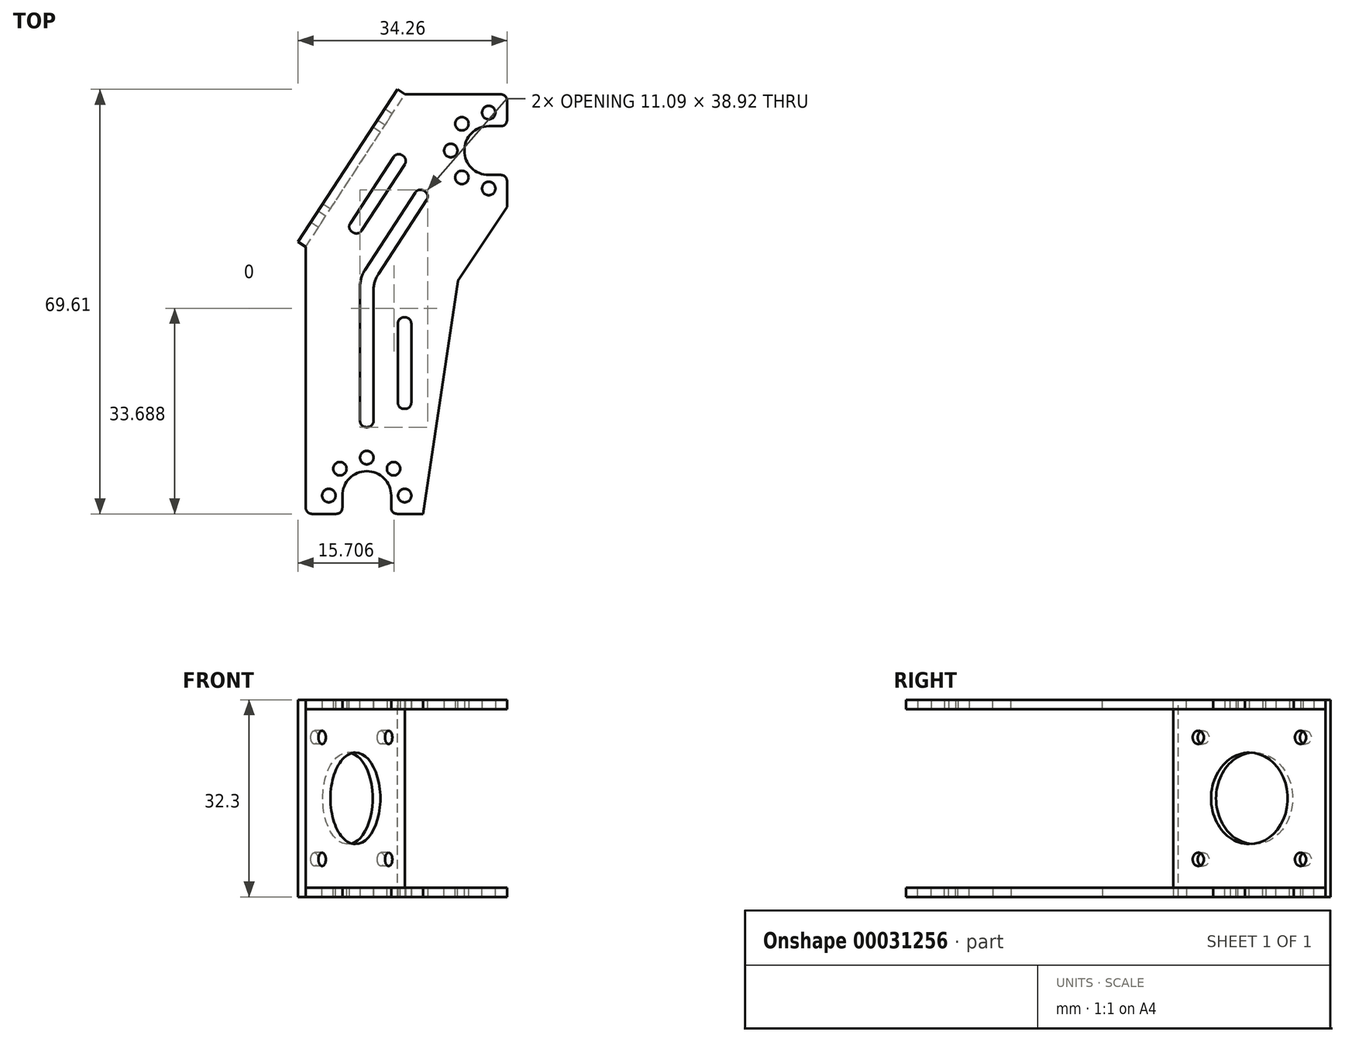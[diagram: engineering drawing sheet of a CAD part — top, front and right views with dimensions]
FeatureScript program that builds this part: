
annotation { "Feature Type Name" : "Feature", "Feature Type Description" : "" }
export const myFeature = defineFeature(function(context is Context, id is Id, definition is map)
    precondition{}
    {
        {
            var Q0;
            Q0=qCreatedBy(makeId("Top.planeOp"),FACE);
            var sketch = newSketch(context, id + "F0", { "sketchPlane" : qUnion([Q0])});
            skLineSegment(sketch, "E0.bottom", {"start": v(-16.5, 34.4) * mm, "end": v(16.5, 34.4) * mm});
            skLineSegment(sketch, "E0.top", {"start": v(-16.5, -34.4) * mm, "end": v(-10.5, -34.4) * mm});
            skLineSegment(sketch, "E0.left", {"start": v(-16.5, 34.4) * mm, "end": v(-16.5, -34.4) * mm});
            skLineSegment(sketch, "E0.right", {"start": v(16.5, 34.4) * mm, "end": v(16.5, 29.17) * mm});
            skPoint(sketch, "E0.middle", {"position": v(0, 0) * mm});
            skArc(sketch, "E1", {"start": v(13.5, 29.17) * mm, "mid": v(9.5, 25.17) * mm, "end": v(13.5, 21.17) * mm});
            skArc(sketch, "E2", {"start": v(-2.5, -31.4) * mm, "mid": v(-6.5, -27.4) * mm, "end": v(-10.5, -31.4) * mm});
            skLineSegment(sketch, "E3.bottom", {"start": v(9.1, 29.57) * mm, "end": v(17.9, 29.57) * mm, "construction": true});
            skLineSegment(sketch, "E3.top", {"start": v(9.1, 20.77) * mm, "end": v(17.9, 20.77) * mm, "construction": true});
            skLineSegment(sketch, "E3.left", {"start": v(9.1, 29.57) * mm, "end": v(9.1, 20.77) * mm, "construction": true});
            skLineSegment(sketch, "E3.right", {"start": v(17.9, 29.57) * mm, "end": v(17.9, 20.77) * mm, "construction": true});
            skCircle(sketch, "E4", {"center": v(9.1, 29.57) * mm, "radius": 1.1 * mm});
            skCircle(sketch, "E5.1.0", {"center": v(7.28, 25.17) * mm, "radius": 1.1 * mm});
            skCircle(sketch, "E5.2.0", {"center": v(9.1, 20.77) * mm, "radius": 1.1 * mm});
            skCircle(sketch, "E5.3.0", {"center": v(13.5, 18.95) * mm, "radius": 1.1 * mm});
            skCircle(sketch, "E5.7.0", {"center": v(13.5, 31.4) * mm, "radius": 1.1 * mm});
            skLineSegment(sketch, "E6.bottom", {"start": v(-10.9, -27) * mm, "end": v(-2.1, -27) * mm, "construction": true});
            skLineSegment(sketch, "E6.top", {"start": v(-10.9, -35.8) * mm, "end": v(-2.1, -35.8) * mm, "construction": true});
            skLineSegment(sketch, "E6.left", {"start": v(-10.9, -27) * mm, "end": v(-10.9, -35.8) * mm, "construction": true});
            skLineSegment(sketch, "E6.right", {"start": v(-2.1, -27) * mm, "end": v(-2.1, -35.8) * mm, "construction": true});
            skCircle(sketch, "E7", {"center": v(-2.1, -27) * mm, "radius": 1.1 * mm});
            skCircle(sketch, "E8.1.0", {"center": v(-6.5, -25.17) * mm, "radius": 1.1 * mm});
            skCircle(sketch, "E8.2.0", {"center": v(-10.9, -27) * mm, "radius": 1.1 * mm});
            skCircle(sketch, "E8.3.0", {"center": v(-12.72, -31.4) * mm, "radius": 1.1 * mm});
            skCircle(sketch, "E8.7.0", {"center": v(-0.28, -31.4) * mm, "radius": 1.1 * mm});
            skLineSegment(sketch, "E9", {"start": v(13.5, 29.17) * mm, "end": v(16.5, 29.17) * mm});
            skLineSegment(sketch, "E10", {"start": v(13.5, 21.17) * mm, "end": v(16.5, 21.17) * mm});
            skLineSegment(sketch, "E11.trimOffspring", {"start": v(16.5, 21.17) * mm, "end": v(16.5, -34.4) * mm});
            skLineSegment(sketch, "E12", {"start": v(-2.5, -31.4) * mm, "end": v(-2.5, -34.4) * mm});
            skLineSegment(sketch, "E13", {"start": v(-10.5, -31.4) * mm, "end": v(-10.5, -34.4) * mm});
            skLineSegment(sketch, "E14.trimOffspring", {"start": v(-2.5, -34.4) * mm, "end": v(16.5, -34.4) * mm});
            skSolve(sketch);
        }
        {
            var Q0;
            Q0 = qSketchRegion(id + "F0", true);
            extrude(context, id + "F1", {"entities" : qUnion([Q0]), "depth" : 1.5 * mm});
        }
        {
            var Q0;
            Q0=makeQuery(id+"F1.opExtrude","CAP_FACE",FACE,{"disambiguationData":[OSD([sQuery(id+"F0.wireOp",EDGE,"E0.bottom"),sQuery(id+"F0.wireOp",EDGE,"E0.top"),sQuery(id+"F0.wireOp",EDGE,"E0.left"),sQuery(id+"F0.wireOp",EDGE,"E0.right"),sQuery(id+"F0.wireOp",EDGE,"E1"),sQuery(id+"F0.wireOp",EDGE,"E2"),sQuery(id+"F0.wireOp",EDGE,"E4"),sQuery(id+"F0.wireOp",EDGE,"E5.1.0"),sQuery(id+"F0.wireOp",EDGE,"E5.2.0"),sQuery(id+"F0.wireOp",EDGE,"E5.3.0"),sQuery(id+"F0.wireOp",EDGE,"E5.7.0"),sQuery(id+"F0.wireOp",EDGE,"E7"),sQuery(id+"F0.wireOp",EDGE,"E8.1.0"),sQuery(id+"F0.wireOp",EDGE,"E8.2.0"),sQuery(id+"F0.wireOp",EDGE,"E8.3.0"),sQuery(id+"F0.wireOp",EDGE,"E8.7.0"),sQuery(id+"F0.wireOp",EDGE,"E9"),sQuery(id+"F0.wireOp",EDGE,"E10"),sQuery(id+"F0.wireOp",EDGE,"E11.trimOffspring"),sQuery(id+"F0.wireOp",EDGE,"E12"),sQuery(id+"F0.wireOp",EDGE,"E13"),sQuery(id+"F0.wireOp",EDGE,"E14.trimOffspring")])],"isStart":false});
            var sketch = newSketch(context, id + "F2", { "sketchPlane" : qUnion([Q0])});
            skPoint(sketch, "E15", {"position": v(7.28, 25.17) * mm});
            skPoint(sketch, "E16", {"position": v(-0.28, -31.4) * mm});
            skLineSegment(sketch, "E17", {"start": v(-0.22, 34.4) * mm, "end": v(-16.5, 9.4) * mm});
            skPoint(sketch, "E18", {"position": v(13.5, 18.95) * mm});
            skLineSegment(sketch, "E19", {"start": v(16.5, 15.95) * mm, "end": v(8.5, 3.95) * mm});
            skLineSegment(sketch, "E20", {"start": v(8.5, 3.95) * mm, "end": v(2.72, -34.4) * mm});
            skPoint(sketch, "E21", {"position": v(13.5, 25.17) * mm});
            skPoint(sketch, "E22", {"position": v(-6.5, -31.4) * mm});
            skLineSegment(sketch, "E23", {"start": v(13.5, 25.17) * mm, "end": v(-6.5, -31.4) * mm, "construction": true});
            skLineSegment(sketch, "E24", {"start": v(0.31, -7.62) * mm, "end": v(-2.35, -15.17) * mm});
            skPoint(sketch, "E25", {"position": v(-1.02, -11.4) * mm});
            skLineSegment(sketch, "E26", {"start": v(1.59, -7.01) * mm, "end": v(2.06, -7.18) * mm});
            skLineSegment(sketch, "E27", {"start": v(-1.74, -16.44) * mm, "end": v(-1.27, -16.6) * mm});
            skLineSegment(sketch, "E28.MirrorCS", {"start": v(2.53, -7.35) * mm, "end": v(2.06, -7.18) * mm});
            skLineSegment(sketch, "E29.MirrorCS", {"start": v(3.14, -8.62) * mm, "end": v(0.48, -16.17) * mm});
            skLineSegment(sketch, "E30.MirrorCS", {"start": v(-0.8, -16.78) * mm, "end": v(-1.27, -16.6) * mm});
            skPoint(sketch, "E31.visualSharp", {"position": v(0.65, -6.68) * mm});
            skArc(sketch, "E31.filletArc", {"start": v(1.59, -7.01) * mm, "mid": v(0.83, -7.06) * mm, "end": v(0.31, -7.62) * mm});
            skPoint(sketch, "E32.visualSharp", {"position": v(-2.69, -16.1) * mm});
            skArc(sketch, "E32.filletArc", {"start": v(-2.35, -15.17) * mm, "mid": v(-2.31, -15.93) * mm, "end": v(-1.74, -16.44) * mm});
            skPoint(sketch, "E33.visualSharp", {"position": v(3.48, -7.68) * mm});
            skArc(sketch, "E33.filletArc", {"start": v(3.14, -8.62) * mm, "mid": v(3.1, -7.86) * mm, "end": v(2.53, -7.35) * mm});
            skPoint(sketch, "E34.visualSharp", {"position": v(0.14, -17.1) * mm});
            skArc(sketch, "E34.filletArc", {"start": v(-0.8, -16.78) * mm, "mid": v(-0.04, -16.74) * mm, "end": v(0.48, -16.17) * mm});
            skSolve(sketch);
        }
        {
            var Q0;
            {var subQ0=sQuery(id+"F2.wireOp",EDGE,"E19");Q0=makeQuery(id+"F2.imprint","IMPRINT",FACE,{"disambiguationData":[TD([[makeQuery(id+"F2.imprint","IMPRINT",EDGE,{"derivedFrom":subQ0}),1.0]])]});}
            var Q1;
            {var subQ0=sQuery(id+"F2.wireOp",EDGE,"E17");Q1=makeQuery(id+"F2.imprint","IMPRINT",FACE,{"disambiguationData":[TD([[makeQuery(id+"F2.imprint","IMPRINT",EDGE,{"derivedFrom":subQ0}),-1.0]])]});}
            extrude(context, id + "F3", {"entities" : qUnion([Q0, Q1]), "operationType" : NewBodyOperationType.REMOVE, "endBound" : BoundingType.UP_TO_NEXT, "oppositeDirection" : true, "depth" : 25 * mm});
        }
        {
            var Q0;
            Q0=makeQuery(id+"F1.opExtrude","CAP_FACE",FACE,{"disambiguationData":[OSD([sQuery(id+"F0.wireOp",EDGE,"E0.bottom"),sQuery(id+"F0.wireOp",EDGE,"E0.top"),sQuery(id+"F0.wireOp",EDGE,"E0.left"),sQuery(id+"F0.wireOp",EDGE,"E0.right"),sQuery(id+"F0.wireOp",EDGE,"E1"),sQuery(id+"F0.wireOp",EDGE,"E2"),sQuery(id+"F0.wireOp",EDGE,"E4"),sQuery(id+"F0.wireOp",EDGE,"E5.1.0"),sQuery(id+"F0.wireOp",EDGE,"E5.2.0"),sQuery(id+"F0.wireOp",EDGE,"E5.3.0"),sQuery(id+"F0.wireOp",EDGE,"E5.7.0"),sQuery(id+"F0.wireOp",EDGE,"E7"),sQuery(id+"F0.wireOp",EDGE,"E8.1.0"),sQuery(id+"F0.wireOp",EDGE,"E8.2.0"),sQuery(id+"F0.wireOp",EDGE,"E8.3.0"),sQuery(id+"F0.wireOp",EDGE,"E8.7.0"),sQuery(id+"F0.wireOp",EDGE,"E9"),sQuery(id+"F0.wireOp",EDGE,"E10"),sQuery(id+"F0.wireOp",EDGE,"E11.trimOffspring"),sQuery(id+"F0.wireOp",EDGE,"E12"),sQuery(id+"F0.wireOp",EDGE,"E13"),sQuery(id+"F0.wireOp",EDGE,"E14.trimOffspring")])],"isStart":false});
            var sketch = newSketch(context, id + "F4", { "sketchPlane" : qUnion([Q0])});
            skPoint(sketch, "E35", {"position": v(13.5, 25.17) * mm});
            skPoint(sketch, "E36", {"position": v(-6.5, -31.4) * mm});
            skPoint(sketch, "E37", {"position": v(7.28, 25.17) * mm});
            skPoint(sketch, "E38", {"position": v(-6.5, -25.17) * mm});
            skLineSegment(sketch, "E39", {"start": v(-6.5, -25.17) * mm, "end": v(-6.5, 4.01) * mm, "construction": true});
            skLineSegment(sketch, "E40", {"start": v(-6.5, 4.01) * mm, "end": v(7.28, 25.17) * mm, "construction": true});
            skLineSegment(sketch, "E41", {"start": v(1.49, 18.3) * mm, "end": v(-6.8, 5.58) * mm});
            skLineSegment(sketch, "E42", {"start": v(-7.6, 2.85) * mm, "end": v(-7.6, -19.17) * mm});
            skLineSegment(sketch, "E43", {"start": v(2.87, 18.59) * mm, "end": v(2.95, 18.53) * mm});
            skLineSegment(sketch, "E44", {"start": v(-6.6, -20.17) * mm, "end": v(-6.5, -20.17) * mm});
            skLineSegment(sketch, "E45.MirrorCS", {"start": v(-6.4, -20.17) * mm, "end": v(-6.5, -20.17) * mm});
            skLineSegment(sketch, "E46.MirrorCS", {"start": v(-5.4, 2.2) * mm, "end": v(-5.4, -19.17) * mm});
            skLineSegment(sketch, "E47.MirrorCS", {"start": v(3.33, 17.1) * mm, "end": v(-4.6, 4.93) * mm});
            skLineSegment(sketch, "E48.MirrorCS", {"start": v(3.04, 18.48) * mm, "end": v(2.95, 18.53) * mm});
            skPoint(sketch, "E49.orphan", {"position": v(-5.4, 4.34) * mm});
            skPoint(sketch, "E50.orphan", {"position": v(-5.76, 3.14) * mm});
            skPoint(sketch, "E51.visualSharp", {"position": v(2.03, 19.13) * mm});
            skArc(sketch, "E51.filletArc", {"start": v(2.87, 18.59) * mm, "mid": v(2.12, 18.73) * mm, "end": v(1.49, 18.3) * mm});
            skPoint(sketch, "E52.visualSharp", {"position": v(3.88, 17.93) * mm});
            skArc(sketch, "E52.filletArc", {"start": v(3.33, 17.1) * mm, "mid": v(3.47, 17.85) * mm, "end": v(3.04, 18.48) * mm});
            skPoint(sketch, "E53.visualSharp", {"position": v(-7.6, -20.17) * mm});
            skArc(sketch, "E53.filletArc", {"start": v(-7.6, -19.17) * mm, "mid": v(-7.3, -19.88) * mm, "end": v(-6.6, -20.17) * mm});
            skPoint(sketch, "E54.visualSharp", {"position": v(-5.4, -20.17) * mm});
            skArc(sketch, "E54.filletArc", {"start": v(-6.4, -20.17) * mm, "mid": v(-5.7, -19.88) * mm, "end": v(-5.4, -19.17) * mm});
            skPoint(sketch, "E55.visualSharp", {"position": v(-7.6, 4.34) * mm});
            skArc(sketch, "E55.filletArc", {"start": v(-6.8, 5.58) * mm, "mid": v(-7.4, 4.28) * mm, "end": v(-7.6, 2.85) * mm});
            skPoint(sketch, "E56.visualSharp", {"position": v(-5.4, 3.69) * mm});
            skArc(sketch, "E56.filletArc", {"start": v(-4.6, 4.93) * mm, "mid": v(-5.2, 3.62) * mm, "end": v(-5.4, 2.2) * mm});
            skLineSegment(sketch, "E57", {"start": v(-0.27, 22.93) * mm, "end": v(-7.36, 12.03) * mm});
            skLineSegment(sketch, "E58", {"start": v(-8.75, 11.74) * mm, "end": v(-8.91, 11.85) * mm});
            skLineSegment(sketch, "E59", {"start": v(-0.56, 24.31) * mm, "end": v(-0.73, 24.42) * mm});
            skLineSegment(sketch, "E60", {"start": v(-2.11, 24.13) * mm, "end": v(-9.2, 13.23) * mm});
            skPoint(sketch, "E61.visualSharp", {"position": v(-1.57, 24.97) * mm});
            skArc(sketch, "E61.filletArc", {"start": v(-0.73, 24.42) * mm, "mid": v(-1.48, 24.56) * mm, "end": v(-2.11, 24.13) * mm});
            skPoint(sketch, "E62.visualSharp", {"position": v(-9.75, 12.4) * mm});
            skArc(sketch, "E62.filletArc", {"start": v(-9.2, 13.23) * mm, "mid": v(-9.35, 12.48) * mm, "end": v(-8.91, 11.85) * mm});
            skPoint(sketch, "E63.visualSharp", {"position": v(0.28, 23.77) * mm});
            skArc(sketch, "E63.filletArc", {"start": v(-0.27, 22.93) * mm, "mid": v(-0.13, 23.68) * mm, "end": v(-0.56, 24.31) * mm});
            skPoint(sketch, "E64.visualSharp", {"position": v(-7.9, 11.2) * mm});
            skArc(sketch, "E64.filletArc", {"start": v(-8.75, 11.74) * mm, "mid": v(-8, 11.6) * mm, "end": v(-7.36, 12.03) * mm});
            skLineSegment(sketch, "E65.bottom", {"start": v(-0.4, -2.17) * mm, "end": v(-0.2, -2.17) * mm});
            skLineSegment(sketch, "E65.top", {"start": v(-0.4, -17.17) * mm, "end": v(-0.2, -17.17) * mm});
            skLineSegment(sketch, "E65.left", {"start": v(-1.4, -3.17) * mm, "end": v(-1.4, -16.17) * mm});
            skLineSegment(sketch, "E65.right", {"start": v(0.8, -3.17) * mm, "end": v(0.8, -16.17) * mm});
            skPoint(sketch, "E65.middle", {"position": v(-0.3, -9.67) * mm});
            skPoint(sketch, "E66.visualSharp", {"position": v(-1.4, -2.17) * mm});
            skArc(sketch, "E66.filletArc", {"start": v(-0.4, -2.17) * mm, "mid": v(-1.1, -2.47) * mm, "end": v(-1.4, -3.17) * mm});
            skPoint(sketch, "E67.visualSharp", {"position": v(-1.4, -17.17) * mm});
            skArc(sketch, "E67.filletArc", {"start": v(-1.4, -16.17) * mm, "mid": v(-1.1, -16.88) * mm, "end": v(-0.4, -17.17) * mm});
            skPoint(sketch, "E68.visualSharp", {"position": v(0.8, -17.17) * mm});
            skArc(sketch, "E68.filletArc", {"start": v(-0.2, -17.17) * mm, "mid": v(0.5, -16.88) * mm, "end": v(0.8, -16.17) * mm});
            skPoint(sketch, "E69.visualSharp", {"position": v(0.8, -2.17) * mm});
            skArc(sketch, "E69.filletArc", {"start": v(0.8, -3.17) * mm, "mid": v(0.5, -2.47) * mm, "end": v(-0.2, -2.17) * mm});
            skLineSegment(sketch, "E70.MirrorCS", {"start": v(1.48, 5.08) * mm, "end": v(1.64, 4.98) * mm, "construction": true});
            skLineSegment(sketch, "E71.MirrorCS", {"start": v(9.66, 17.65) * mm, "end": v(9.83, 17.55) * mm, "construction": true});
            skArc(sketch, "E72.MirrorCS", {"start": v(3.03, 5.27) * mm, "mid": v(2.4, 4.83) * mm, "end": v(1.64, 4.98) * mm, "construction": true});
            skArc(sketch, "E73.MirrorCS", {"start": v(8.28, 17.36) * mm, "mid": v(8.9, 17.8) * mm, "end": v(9.66, 17.65) * mm, "construction": true});
            skArc(sketch, "E74.MirrorCS", {"start": v(9.83, 17.55) * mm, "mid": v(10.26, 16.91) * mm, "end": v(10.12, 16.16) * mm, "construction": true});
            skArc(sketch, "E75.MirrorCS", {"start": v(1.48, 5.08) * mm, "mid": v(1.04, 5.72) * mm, "end": v(1.18, 6.47) * mm, "construction": true});
            skLineSegment(sketch, "E76.MirrorCS", {"start": v(10.12, 16.16) * mm, "end": v(3.03, 5.27) * mm, "construction": true});
            skPoint(sketch, "E77.MirrorP", {"position": v(10.67, 17) * mm});
            skPoint(sketch, "E78.MirrorP", {"position": v(8.82, 18.2) * mm});
            skLineSegment(sketch, "E79.MirrorCS", {"start": v(8.28, 17.36) * mm, "end": v(1.18, 6.47) * mm, "construction": true});
            skPoint(sketch, "E80.MirrorP", {"position": v(2.48, 4.43) * mm});
            skPoint(sketch, "E81.MirrorP", {"position": v(0.64, 5.63) * mm});
            skLineSegment(sketch, "E82.MirrorCS", {"start": v(-12.6, -17.17) * mm, "end": v(-12.8, -17.17) * mm, "construction": true});
            skLineSegment(sketch, "E83.MirrorCS", {"start": v(-12.6, -2.17) * mm, "end": v(-12.8, -2.17) * mm, "construction": true});
            skArc(sketch, "E84.MirrorCS", {"start": v(-12.8, -17.17) * mm, "mid": v(-13.5, -16.88) * mm, "end": v(-13.8, -16.17) * mm, "construction": true});
            skArc(sketch, "E85.MirrorCS", {"start": v(-13.8, -3.17) * mm, "mid": v(-13.5, -2.47) * mm, "end": v(-12.8, -2.17) * mm, "construction": true});
            skArc(sketch, "E86.MirrorCS", {"start": v(-12.6, -2.17) * mm, "mid": v(-11.9, -2.47) * mm, "end": v(-11.6, -3.17) * mm, "construction": true});
            skArc(sketch, "E87.MirrorCS", {"start": v(-11.6, -16.17) * mm, "mid": v(-11.9, -16.88) * mm, "end": v(-12.6, -17.17) * mm, "construction": true});
            skPoint(sketch, "E88.MirrorP", {"position": v(-13.8, -17.17) * mm});
            skPoint(sketch, "E89.MirrorP", {"position": v(-13.8, -2.17) * mm});
            skLineSegment(sketch, "E90.MirrorCS", {"start": v(-11.6, -3.17) * mm, "end": v(-11.6, -16.17) * mm, "construction": true});
            skPoint(sketch, "E91.MirrorP", {"position": v(-12.7, -9.67) * mm});
            skPoint(sketch, "E92.MirrorP", {"position": v(-11.6, -2.17) * mm});
            skPoint(sketch, "E93.MirrorP", {"position": v(-11.6, -17.17) * mm});
            skLineSegment(sketch, "E94.MirrorCS", {"start": v(-13.8, -3.17) * mm, "end": v(-13.8, -16.17) * mm, "construction": true});
            skPoint(sketch, "E95.0.1.0", {"position": v(-11.6, -7.17) * mm});
            skPoint(sketch, "E95.0.1.1", {"position": v(-11.6, 7.83) * mm});
            skPoint(sketch, "E95.0.1.2", {"position": v(-12.7, 0.33) * mm});
            skLineSegment(sketch, "E95.0.1.3", {"start": v(-13.8, 6.83) * mm, "end": v(-13.8, -6.17) * mm});
            skPoint(sketch, "E95.0.1.4", {"position": v(-13.8, -7.17) * mm});
            skLineSegment(sketch, "E95.0.1.5", {"start": v(-11.6, 6.83) * mm, "end": v(-11.6, -6.17) * mm});
            skPoint(sketch, "E95.0.1.6", {"position": v(-13.8, 7.83) * mm});
            skArc(sketch, "E95.0.1.7", {"start": v(-12.8, -7.17) * mm, "mid": v(-13.5, -6.88) * mm, "end": v(-13.8, -6.17) * mm});
            skArc(sketch, "E95.0.1.8", {"start": v(-13.8, 6.83) * mm, "mid": v(-13.5, 7.53) * mm, "end": v(-12.8, 7.83) * mm});
            skArc(sketch, "E95.0.1.9", {"start": v(-12.6, 7.83) * mm, "mid": v(-11.9, 7.53) * mm, "end": v(-11.6, 6.83) * mm});
            skArc(sketch, "E95.0.1.10", {"start": v(-11.6, -6.17) * mm, "mid": v(-11.9, -6.88) * mm, "end": v(-12.6, -7.17) * mm});
            skLineSegment(sketch, "E95.0.1.11", {"start": v(-12.6, 7.83) * mm, "end": v(-12.8, 7.83) * mm});
            skLineSegment(sketch, "E95.0.1.12", {"start": v(-12.6, -7.17) * mm, "end": v(-12.8, -7.17) * mm});
            skLineSegment(sketch, "E95.direction1", {"start": v(-13.8, -17.17) * mm, "end": v(11.2, -17.17) * mm, "construction": true});
            skLineSegment(sketch, "E95.direction2", {"start": v(-13.8, -17.17) * mm, "end": v(-13.8, -7.17) * mm, "construction": true});
            skLineSegment(sketch, "E96.1.0.0", {"start": v(2.82, 8.98) * mm, "end": v(-4.27, -1.91) * mm});
            skArc(sketch, "E96.1.0.1", {"start": v(2.82, 8.98) * mm, "mid": v(3.45, 9.41) * mm, "end": v(4.2, 9.27) * mm});
            skArc(sketch, "E96.1.0.2", {"start": v(4.37, 9.17) * mm, "mid": v(4.8, 8.53) * mm, "end": v(4.66, 7.78) * mm});
            skLineSegment(sketch, "E96.1.0.3", {"start": v(4.2, 9.27) * mm, "end": v(4.37, 9.17) * mm});
            skLineSegment(sketch, "E96.1.0.4", {"start": v(4.66, 7.78) * mm, "end": v(-2.43, -3.11) * mm});
            skArc(sketch, "E96.1.0.5", {"start": v(-3.98, -3.3) * mm, "mid": v(-4.41, -2.66) * mm, "end": v(-4.27, -1.91) * mm});
            skLineSegment(sketch, "E96.1.0.6", {"start": v(-3.98, -3.3) * mm, "end": v(-3.81, -3.4) * mm});
            skArc(sketch, "E96.1.0.7", {"start": v(-2.43, -3.11) * mm, "mid": v(-3.06, -3.55) * mm, "end": v(-3.81, -3.4) * mm});
            skLineSegment(sketch, "E96.direction1", {"start": v(-3.98, -3.3) * mm, "end": v(1.48, 5.08) * mm, "construction": true});
            skSolve(sketch);
        }
        {
            var Q0;
            Q0=makeQuery(id+"F4.imprint","IMPRINT",FACE,{"disambiguationData":[TD([[makeQuery(id+"F4.imprint","IMPRINT",EDGE,{"derivedFrom":sQuery(id+"F4.wireOp",EDGE,"E57")}),-1.0]])]});
            var Q1;
            Q1=makeQuery(id+"F4.imprint","IMPRINT",FACE,{"disambiguationData":[TD([[makeQuery(id+"F4.imprint","IMPRINT",EDGE,{"derivedFrom":sQuery(id+"F4.wireOp",EDGE,"E41")}),1.0]])]});
            var Q2;
            Q2=makeQuery(id+"F4.imprint","IMPRINT",FACE,{"disambiguationData":[TD([[makeQuery(id+"F4.imprint","IMPRINT",EDGE,{"derivedFrom":sQuery(id+"F4.wireOp",EDGE,"E65.bottom")}),-1.0]])]});
            extrude(context, id + "F5", {"entities" : qUnion([Q0, Q1, Q2]), "operationType" : NewBodyOperationType.REMOVE, "endBound" : BoundingType.UP_TO_NEXT, "oppositeDirection" : true, "depth" : 25 * mm});
        }
        {
            var Q0;
            Q0=makeQuery(id+"F1.opExtrude","SWEPT_EDGE",EDGE,{"disambiguationData":[OSD([sQuery(id+"F0.wireOp",EDGE,"E0.top"),sQuery(id+"F0.wireOp",EDGE,"E0.left")])]});
            var Q1;
            Q1=makeQuery(id+"F1.opExtrude","SWEPT_EDGE",EDGE,{"disambiguationData":[OSD([sQuery(id+"F0.wireOp",EDGE,"E0.top"),sQuery(id+"F0.wireOp",EDGE,"E13")])]});
            var Q2;
            Q2=makeQuery(id+"F1.opExtrude","SWEPT_EDGE",EDGE,{"disambiguationData":[OSD([sQuery(id+"F0.wireOp",EDGE,"E12"),sQuery(id+"F0.wireOp",EDGE,"E14.trimOffspring")])]});
            var Q3;
            Q3=makeQuery(id+"F3.boolean.opBoolean","COPY",EDGE,{"derivedFrom":makeQuery(id+"F3.opExtrude","SWEPT_EDGE",EDGE,{"disambiguationData":[OSD([sQuery(id+"F0.wireOp",EDGE,"E14.trimOffspring"),sQuery(id+"F2.wireOp",EDGE,"E20")])]})});
            var Q4;
            Q4=makeQuery(id+"F3.boolean.opBoolean","COPY",EDGE,{"derivedFrom":makeQuery(id+"F3.opExtrude","SWEPT_EDGE",EDGE,{"disambiguationData":[OSD([sQuery(id+"F2.wireOp",EDGE,"E19"),sQuery(id+"F2.wireOp",EDGE,"E20")])]})});
            var Q5;
            Q5=makeQuery(id+"F3.boolean.opBoolean","COPY",EDGE,{"derivedFrom":makeQuery(id+"F3.opExtrude","SWEPT_EDGE",EDGE,{"disambiguationData":[OSD([sQuery(id+"F0.wireOp",EDGE,"E11.trimOffspring"),sQuery(id+"F2.wireOp",EDGE,"E19")])]})});
            var Q6;
            Q6=makeQuery(id+"F1.opExtrude","SWEPT_EDGE",EDGE,{"disambiguationData":[OSD([sQuery(id+"F0.wireOp",EDGE,"E0.bottom"),sQuery(id+"F0.wireOp",EDGE,"E0.right")])]});
            var Q7;
            Q7=makeQuery(id+"F1.opExtrude","SWEPT_EDGE",EDGE,{"disambiguationData":[OSD([sQuery(id+"F0.wireOp",EDGE,"E10"),sQuery(id+"F0.wireOp",EDGE,"E11.trimOffspring")])]});
            var Q8;
            Q8=makeQuery(id+"F1.opExtrude","SWEPT_EDGE",EDGE,{"disambiguationData":[OSD([sQuery(id+"F0.wireOp",EDGE,"E0.right"),sQuery(id+"F0.wireOp",EDGE,"E9")])]});
            fillet(context, id + "F6", {"entities" : qUnion([Q0, Q1, Q2, Q3, Q4, Q5, Q6, Q7, Q8]), "radius" : 1 * mm, "tangentPropagation" : true, "allowEdgeOverflow" : false});
        }
        {
            var Q0;
            Q0=makeQuery(id+"F1.opExtrude","CAP_FACE",FACE,{"disambiguationData":[OSD([sQuery(id+"F0.wireOp",EDGE,"E0.bottom"),sQuery(id+"F0.wireOp",EDGE,"E0.top"),sQuery(id+"F0.wireOp",EDGE,"E0.left"),sQuery(id+"F0.wireOp",EDGE,"E0.right"),sQuery(id+"F0.wireOp",EDGE,"E1"),sQuery(id+"F0.wireOp",EDGE,"E2"),sQuery(id+"F0.wireOp",EDGE,"E4"),sQuery(id+"F0.wireOp",EDGE,"E5.1.0"),sQuery(id+"F0.wireOp",EDGE,"E5.2.0"),sQuery(id+"F0.wireOp",EDGE,"E5.3.0"),sQuery(id+"F0.wireOp",EDGE,"E5.7.0"),sQuery(id+"F0.wireOp",EDGE,"E7"),sQuery(id+"F0.wireOp",EDGE,"E8.1.0"),sQuery(id+"F0.wireOp",EDGE,"E8.2.0"),sQuery(id+"F0.wireOp",EDGE,"E8.3.0"),sQuery(id+"F0.wireOp",EDGE,"E8.7.0"),sQuery(id+"F0.wireOp",EDGE,"E9"),sQuery(id+"F0.wireOp",EDGE,"E10"),sQuery(id+"F0.wireOp",EDGE,"E11.trimOffspring"),sQuery(id+"F0.wireOp",EDGE,"E12"),sQuery(id+"F0.wireOp",EDGE,"E13"),sQuery(id+"F0.wireOp",EDGE,"E14.trimOffspring")])],"isStart":false});
            var sketch = newSketch(context, id + "F7", { "sketchPlane" : qUnion([Q0])});
            skLineSegment(sketch, "E97", {"start": v(-16.5, 9.4) * mm, "end": v(-0.22, 34.4) * mm});
            skLineSegment(sketch, "E98", {"start": v(-0.22, 34.4) * mm, "end": v(-1.48, 35.21) * mm});
            skLineSegment(sketch, "E99", {"start": v(-1.48, 35.21) * mm, "end": v(-17.76, 10.21) * mm});
            skLineSegment(sketch, "E100", {"start": v(-17.76, 10.21) * mm, "end": v(-16.5, 9.4) * mm});
            skSolve(sketch);
        }
        {
            var Q0;
            Q0 = qSketchRegion(id + "F7", true);
            extrude(context, id + "F8", {"entities" : qUnion([Q0]), "operationType" : NewBodyOperationType.ADD, "oppositeDirection" : true, "depth" : (1.5 + 29.3 / 2) * mm});
        }
        {
            var Q0;
            Q0=qCreatedBy(makeId("Top.planeOp"),FACE);
            cPlane(context, id + "F9", {"entities" : qUnion([Q0]), "cplaneType" : CPlaneType.OFFSET, "offset" : (29.3 / 2) * mm, "oppositeDirection" : true, "width" : 150 * mm, "height" : 150 * mm});
        }
        {
            var Q0;
            Q0=makeQuery(id+"F1.opExtrude","SWEPT_BODY",BODY,{"disambiguationData":[OSD([sQuery(id+"F0.wireOp",EDGE,"E0.bottom"),sQuery(id+"F0.wireOp",EDGE,"E0.top"),sQuery(id+"F0.wireOp",EDGE,"E0.left"),sQuery(id+"F0.wireOp",EDGE,"E0.right"),sQuery(id+"F0.wireOp",EDGE,"E1"),sQuery(id+"F0.wireOp",EDGE,"E2"),sQuery(id+"F0.wireOp",EDGE,"E4"),sQuery(id+"F0.wireOp",EDGE,"E5.1.0"),sQuery(id+"F0.wireOp",EDGE,"E5.2.0"),sQuery(id+"F0.wireOp",EDGE,"E5.3.0"),sQuery(id+"F0.wireOp",EDGE,"E5.7.0"),sQuery(id+"F0.wireOp",EDGE,"E7"),sQuery(id+"F0.wireOp",EDGE,"E8.1.0"),sQuery(id+"F0.wireOp",EDGE,"E8.2.0"),sQuery(id+"F0.wireOp",EDGE,"E8.3.0"),sQuery(id+"F0.wireOp",EDGE,"E8.7.0"),sQuery(id+"F0.wireOp",EDGE,"E9"),sQuery(id+"F0.wireOp",EDGE,"E10"),sQuery(id+"F0.wireOp",EDGE,"E11.trimOffspring"),sQuery(id+"F0.wireOp",EDGE,"E12"),sQuery(id+"F0.wireOp",EDGE,"E13"),sQuery(id+"F0.wireOp",EDGE,"E14.trimOffspring")])]});
            var Q1;
            Q1=qCreatedBy(id+"F9.planeOp",FACE);
            mirror(context, id + "F10", {"operationType" : NewBodyOperationType.ADD, "entities" : qUnion([Q0]), "mirrorPlane" : qUnion([Q1])});
        }
        {
            var Q0;
            {var subQ0=makeQuery(id+"F8.opExtrude","SWEPT_FACE",FACE,{"disambiguationData":[OSD([sQuery(id+"F7.wireOp",EDGE,"E99")])]});Q0=makeQuery(id+"F10.boolean.opBoolean","MERGE",FACE,{"derivedFrom":[subQ0,makeQuery(id+"F10.opPattern","COPY",FACE,{"derivedFrom":subQ0,"instanceName":"1"})]});}
            var sketch = newSketch(context, id + "F11", { "sketchPlane" : qUnion([Q0])});
            skLineSegment(sketch, "E101", {"start": v(-13.79, -30.8) * mm, "end": v(-13.79, 1.5) * mm, "construction": true});
            skLineSegment(sketch, "E102.bottom", {"start": v(-23.79, -24.65) * mm, "end": v(-3.79, -24.65) * mm, "construction": true});
            skLineSegment(sketch, "E102.top", {"start": v(-23.79, -4.65) * mm, "end": v(-3.79, -4.65) * mm, "construction": true});
            skLineSegment(sketch, "E102.left", {"start": v(-23.79, -24.65) * mm, "end": v(-23.79, -4.65) * mm, "construction": true});
            skLineSegment(sketch, "E102.right", {"start": v(-3.79, -24.65) * mm, "end": v(-3.79, -4.65) * mm, "construction": true});
            skPoint(sketch, "E102.middle", {"position": v(-13.79, -14.65) * mm});
            skCircle(sketch, "E103", {"center": v(-23.79, -24.65) * mm, "radius": 1.1 * mm});
            skCircle(sketch, "E104.MirrorC", {"center": v(-23.79, -4.65) * mm, "radius": 1.1 * mm});
            skCircle(sketch, "E105.MirrorC", {"center": v(-3.79, -24.65) * mm, "radius": 1.1 * mm});
            skCircle(sketch, "E106.MirrorC", {"center": v(-3.79, -4.65) * mm, "radius": 1.1 * mm});
            skCircle(sketch, "E107", {"center": v(-13.79, -14.65) * mm, "radius": 7.5 * mm});
            skSolve(sketch);
        }
        {
            var Q0;
            Q0 = qSketchRegion(id + "F11", true);
            extrude(context, id + "F12", {"entities" : qUnion([Q0]), "operationType" : NewBodyOperationType.REMOVE, "endBound" : BoundingType.UP_TO_NEXT, "oppositeDirection" : true, "depth" : 25 * mm});
        }
    });
